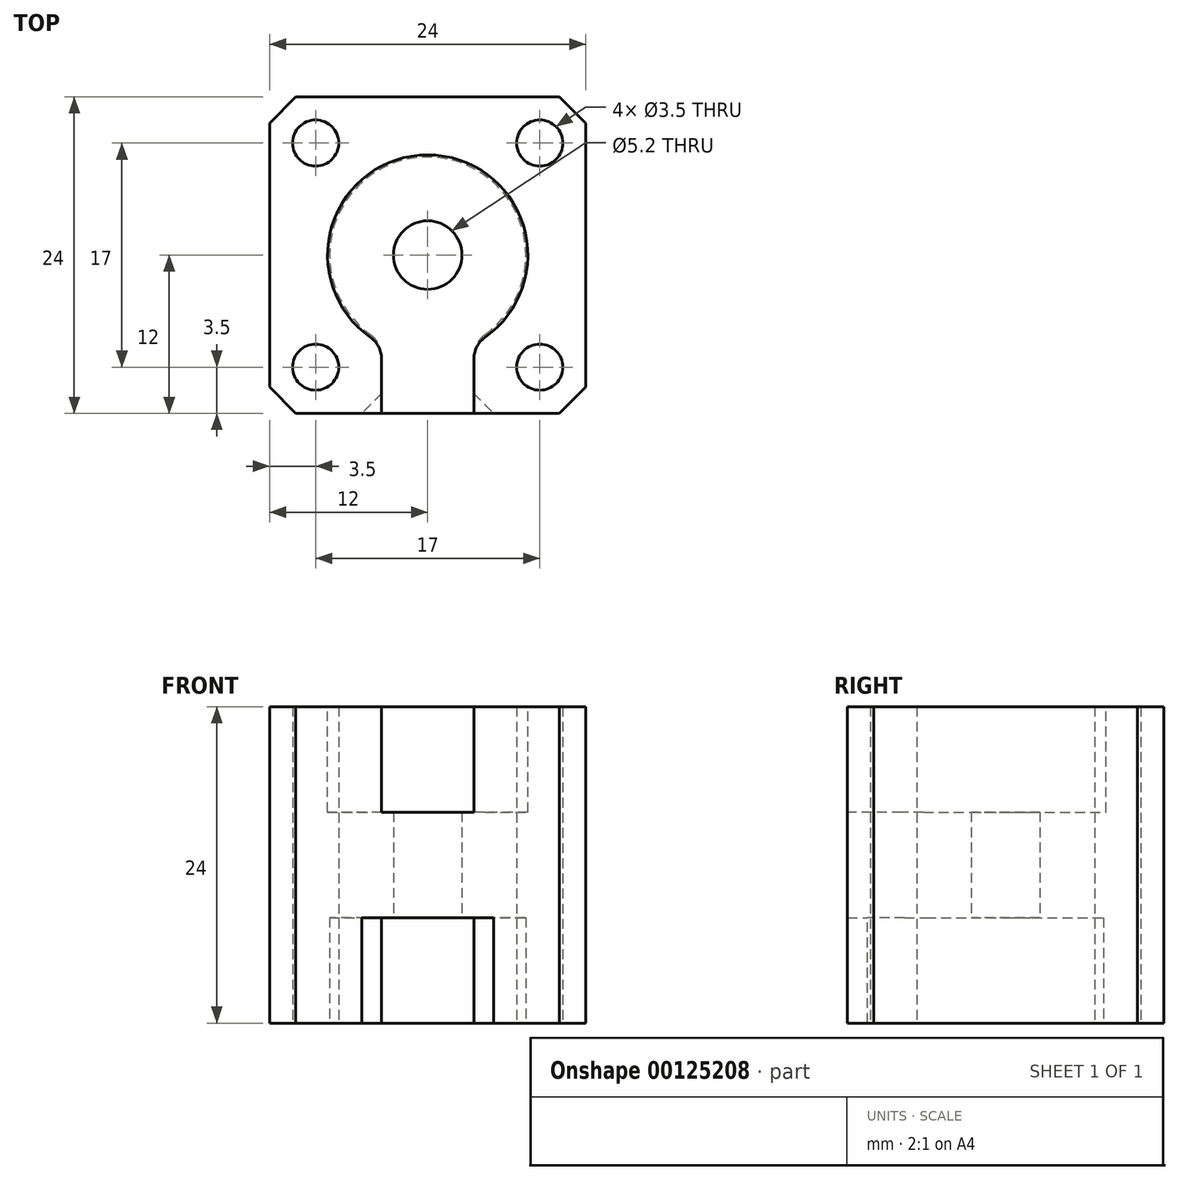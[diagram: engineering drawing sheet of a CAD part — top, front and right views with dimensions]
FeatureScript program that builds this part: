
annotation { "Feature Type Name" : "Feature", "Feature Type Description" : "" }
export const myFeature = defineFeature(function(context is Context, id is Id, definition is map)
    precondition{}
    {
        {
            var Q0;
            Q0=qCreatedBy(makeId("Top.planeOp"),FACE);
            var sketch = newSketch(context, id + "F0", { "sketchPlane" : qUnion([Q0])});
            skLineSegment(sketch, "E0.bottom", {"start": v(-12, 12) * mm, "end": v(12, 12) * mm});
            skLineSegment(sketch, "E0.top", {"start": v(-12, -12) * mm, "end": v(12, -12) * mm});
            skLineSegment(sketch, "E0.left", {"start": v(-12, 12) * mm, "end": v(-12, -12) * mm});
            skLineSegment(sketch, "E0.right", {"start": v(12, 12) * mm, "end": v(12, -12) * mm});
            skCircle(sketch, "E1", {"center": v(0, 0) * mm, "radius": 2.6 * mm});
            skSolve(sketch);
        }
        {
            var Q0;
            Q0 = qSketchRegion(id + "F0", true);
            extrude(context, id + "F1", {"entities" : qUnion([Q0]), "depth" : 24 * mm});
        }
        {
            var Q0;
            Q0=makeQuery(id+"F1.opExtrude","SWEPT_EDGE",EDGE,{"disambiguationData":[OSD([sQuery(id+"F0.wireOp",EDGE,"E0.top"),sQuery(id+"F0.wireOp",EDGE,"E0.left")])]});
            var Q1;
            Q1=makeQuery(id+"F1.opExtrude","SWEPT_EDGE",EDGE,{"disambiguationData":[OSD([sQuery(id+"F0.wireOp",EDGE,"E0.top"),sQuery(id+"F0.wireOp",EDGE,"E0.right")])]});
            var Q2;
            Q2=makeQuery(id+"F1.opExtrude","SWEPT_EDGE",EDGE,{"disambiguationData":[OSD([sQuery(id+"F0.wireOp",EDGE,"E0.bottom"),sQuery(id+"F0.wireOp",EDGE,"E0.left")])]});
            var Q3;
            Q3=makeQuery(id+"F1.opExtrude","SWEPT_EDGE",EDGE,{"disambiguationData":[OSD([sQuery(id+"F0.wireOp",EDGE,"E0.bottom"),sQuery(id+"F0.wireOp",EDGE,"E0.right")])]});
            chamfer(context, id + "F2", {"entities" : qUnion([Q0, Q1, Q2, Q3]), "width" : 2 * mm, "tangentPropagation" : true});
        }
        {
            var Q0;
            Q0=qCreatedBy(makeId("Top.planeOp"),FACE);
            var sketch = newSketch(context, id + "F3", { "sketchPlane" : qUnion([Q0])});
            skCircle(sketch, "E2", {"center": v(0, 0) * mm, "radius": 7.44 * mm});
            skLineSegment(sketch, "E3.bottom", {"start": v(-3.5, -3) * mm, "end": v(3.5, -3) * mm});
            skLineSegment(sketch, "E3.top", {"start": v(-3.5, -13) * mm, "end": v(3.5, -13) * mm});
            skLineSegment(sketch, "E3.left", {"start": v(-3.5, -3) * mm, "end": v(-3.5, -13) * mm});
            skLineSegment(sketch, "E3.right", {"start": v(3.5, -3) * mm, "end": v(3.5, -13) * mm});
            skSolve(sketch);
        }
        {
            var Q0;
            Q0 = qSketchRegion(id + "F3", true);
            extrude(context, id + "F4", {"entities" : qUnion([Q0]), "operationType" : NewBodyOperationType.REMOVE, "depth" : 8 * mm});
        }
        {
            var Q0;
            Q0=makeQuery(id+"F4.boolean.opBoolean","COPY",EDGE,{"derivedFrom":makeQuery(id+"F4.opExtrude","SWEPT_EDGE",EDGE,{"disambiguationData":[OSD([sQuery(id+"F3.wireOp",EDGE,"E2"),sQuery(id+"F3.wireOp",EDGE,"E3.left")])]})});
            var Q1;
            Q1=makeQuery(id+"F4.boolean.opBoolean","COPY",EDGE,{"derivedFrom":makeQuery(id+"F4.opExtrude","SWEPT_EDGE",EDGE,{"disambiguationData":[OSD([sQuery(id+"F3.wireOp",EDGE,"E2"),sQuery(id+"F3.wireOp",EDGE,"E3.right")])]})});
            fillet(context, id + "F5", {"entities" : qUnion([Q0, Q1]), "radius" : 2 * mm, "tangentPropagation" : true, "allowEdgeOverflow" : false});
        }
        {
            var Q0;
            Q0=makeQuery(id+"F1.opExtrude","CAP_FACE",FACE,{"disambiguationData":[OSD([sQuery(id+"F0.wireOp",EDGE,"E0.bottom"),sQuery(id+"F0.wireOp",EDGE,"E0.top"),sQuery(id+"F0.wireOp",EDGE,"E0.left"),sQuery(id+"F0.wireOp",EDGE,"E0.right"),sQuery(id+"F0.wireOp",EDGE,"E1")])],"isStart":false});
            var sketch = newSketch(context, id + "F6", { "sketchPlane" : qUnion([Q0])});
            skCircle(sketch, "E4", {"center": v(0, 0) * mm, "radius": 7.6 * mm});
            skLineSegment(sketch, "E5.bottom", {"start": v(-3.5, -4.01) * mm, "end": v(3.5, -4.01) * mm});
            skLineSegment(sketch, "E5.top", {"start": v(-3.5, -12) * mm, "end": v(3.5, -12) * mm});
            skLineSegment(sketch, "E5.left", {"start": v(-3.5, -4.01) * mm, "end": v(-3.5, -12) * mm});
            skLineSegment(sketch, "E5.right", {"start": v(3.5, -4.01) * mm, "end": v(3.5, -12) * mm});
            skSolve(sketch);
        }
        {
            var Q0;
            Q0 = qSketchRegion(id + "F6", true);
            extrude(context, id + "F7", {"entities" : qUnion([Q0]), "operationType" : NewBodyOperationType.REMOVE, "oppositeDirection" : true, "depth" : 8 * mm});
        }
        {
            var Q0;
            Q0=makeQuery(id+"F7.boolean.opBoolean","COPY",EDGE,{"derivedFrom":makeQuery(id+"F7.opExtrude","SWEPT_EDGE",EDGE,{"disambiguationData":[OSD([sQuery(id+"F6.wireOp",EDGE,"E4"),sQuery(id+"F6.wireOp",EDGE,"E5.right")])]})});
            var Q1;
            Q1=makeQuery(id+"F7.boolean.opBoolean","COPY",EDGE,{"derivedFrom":makeQuery(id+"F7.opExtrude","SWEPT_EDGE",EDGE,{"disambiguationData":[OSD([sQuery(id+"F6.wireOp",EDGE,"E4"),sQuery(id+"F6.wireOp",EDGE,"E5.left")])]})});
            fillet(context, id + "F8", {"entities" : qUnion([Q0, Q1]), "radius" : 2 * mm, "tangentPropagation" : true, "allowEdgeOverflow" : false});
        }
        {
            var Q0;
            Q0=makeQuery(id+"F7.boolean.opBoolean","COPY",EDGE,{"derivedFrom":makeQuery(id+"F7.opExtrude","SWEPT_EDGE",EDGE,{"disambiguationData":[OSD([sQuery(id+"F0.wireOp",EDGE,"E0.top"),sQuery(id+"F6.wireOp",EDGE,"E5.top"),sQuery(id+"F6.wireOp",EDGE,"E5.right")])]})});
            var Q1;
            Q1=makeQuery(id+"F7.boolean.opBoolean","COPY",EDGE,{"derivedFrom":makeQuery(id+"F7.opExtrude","SWEPT_EDGE",EDGE,{"disambiguationData":[OSD([sQuery(id+"F0.wireOp",EDGE,"E0.top"),sQuery(id+"F6.wireOp",EDGE,"E5.top"),sQuery(id+"F6.wireOp",EDGE,"E5.left")])]})});
            var Q2;
            Q2=makeQuery(id+"F4.boolean.opBoolean","INTERSECT",EDGE,{"derivedFrom":[makeQuery(id+"F1.opExtrude","SWEPT_FACE",FACE,{"disambiguationData":[OSD([sQuery(id+"F0.wireOp",EDGE,"E0.top")])]}),makeQuery(id+"F4.opExtrude","SWEPT_FACE",FACE,{"disambiguationData":[OSD([sQuery(id+"F3.wireOp",EDGE,"E3.right")])]})]});
            var Q3;
            Q3=makeQuery(id+"F4.boolean.opBoolean","INTERSECT",EDGE,{"derivedFrom":[makeQuery(id+"F1.opExtrude","SWEPT_FACE",FACE,{"disambiguationData":[OSD([sQuery(id+"F0.wireOp",EDGE,"E0.top")])]}),makeQuery(id+"F4.opExtrude","SWEPT_FACE",FACE,{"disambiguationData":[OSD([sQuery(id+"F3.wireOp",EDGE,"E3.left")])]})]});
            chamfer(context, id + "F9", {"entities" : qUnion([Q0, Q1, Q2, Q3]), "width" : 1.5 * mm, "tangentPropagation" : true});
        }
        {
            var Q0;
            Q0=qCreatedBy(makeId("Top.planeOp"),FACE);
            var sketch = newSketch(context, id + "F10", { "sketchPlane" : qUnion([Q0])});
            skCircle(sketch, "E6", {"center": v(-8.5, -8.5) * mm, "radius": 1.75 * mm});
            skCircle(sketch, "E7", {"center": v(8.5, -8.5) * mm, "radius": 1.75 * mm});
            skCircle(sketch, "E8", {"center": v(8.5, 8.5) * mm, "radius": 1.75 * mm});
            skCircle(sketch, "E9", {"center": v(-8.5, 8.5) * mm, "radius": 1.75 * mm});
            skSolve(sketch);
        }
        {
            var Q0;
            Q0 = qSketchRegion(id + "F10", true);
            extrude(context, id + "F11", {"entities" : qUnion([Q0]), "operationType" : NewBodyOperationType.REMOVE, "depth" : 25 * mm});
        }
    });
